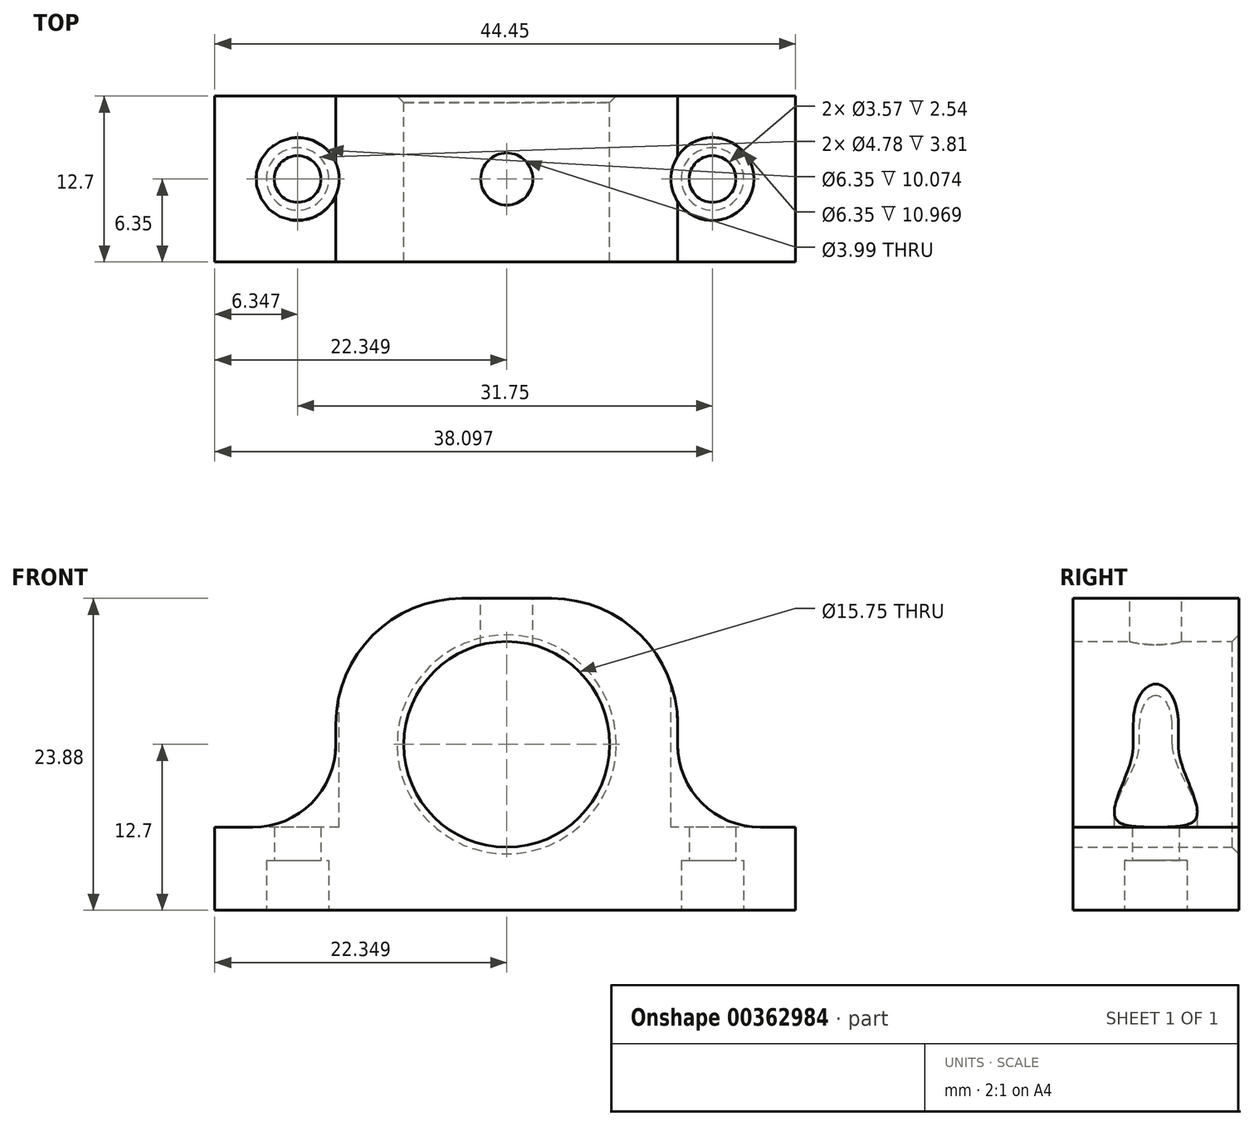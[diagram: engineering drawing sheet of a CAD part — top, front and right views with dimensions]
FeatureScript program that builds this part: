
annotation { "Feature Type Name" : "Feature", "Feature Type Description" : "" }
export const myFeature = defineFeature(function(context is Context, id is Id, definition is map)
    precondition{}
    {
        {
            var Q0;
            Q0=qCreatedBy(makeId("Front.planeOp"),FACE);
            var sketch = newSketch(context, id + "F0", { "sketchPlane" : qUnion([Q0])});
            skLineSegment(sketch, "E0", {"start": v(-60.83, 8) * mm, "end": v(-16.38, 8) * mm});
            skLineSegment(sketch, "E1", {"start": v(-16.38, 8) * mm, "end": v(-16.38, 14.34) * mm});
            skLineSegment(sketch, "E2", {"start": v(-60.83, 8) * mm, "end": v(-60.83, 14.34) * mm});
            skCircle(sketch, "E3", {"center": v(-38.48, 20.7) * mm, "radius": 7.87 * mm});
            skLineSegment(sketch, "E4.0", {"start": v(-25.4, 20.7) * mm, "end": v(-25.4, 22.21) * mm});
            skLineSegment(sketch, "E5.0", {"start": v(-51.56, 20.7) * mm, "end": v(-51.56, 22.21) * mm});
            skLineSegment(sketch, "E6", {"start": v(-57.91, 14.34) * mm, "end": v(-60.83, 14.34) * mm});
            skLineSegment(sketch, "E7", {"start": v(-19.05, 14.34) * mm, "end": v(-16.38, 14.34) * mm});
            skLineSegment(sketch, "E8.0", {"start": v(-41.9, 31.87) * mm, "end": v(-35.05, 31.87) * mm});
            skArc(sketch, "E9.filletArc", {"start": v(-41.9, 31.87) * mm, "mid": v(-48.73, 29.04) * mm, "end": v(-51.56, 22.21) * mm});
            skArc(sketch, "E10.filletArc", {"start": v(-25.4, 22.21) * mm, "mid": v(-28.23, 29.04) * mm, "end": v(-35.05, 31.87) * mm});
            skPoint(sketch, "E11.visualSharp", {"position": v(-25.4, 14.34) * mm});
            skArc(sketch, "E11.filletArc", {"start": v(-25.4, 20.7) * mm, "mid": v(-23.54, 16.2) * mm, "end": v(-19.05, 14.34) * mm});
            skPoint(sketch, "E12.visualSharp", {"position": v(-51.56, 14.34) * mm});
            skArc(sketch, "E12.filletArc", {"start": v(-57.91, 14.34) * mm, "mid": v(-53.42, 16.2) * mm, "end": v(-51.56, 20.7) * mm});
            skSolve(sketch);
        }
        {
            var Q0;
            Q0=makeQuery(id+"F0.imprint","IMPRINT",FACE,{"disambiguationData":[TD([[makeQuery(id+"F0.imprint","IMPRINT",EDGE,{"derivedFrom":sQuery(id+"F0.wireOp",EDGE,"E0")}),1.0]])]});
            extrude(context, id + "F1", {"entities" : qUnion([Q0]), "depth" : 12.7 * mm});
        }
        {
            var Q0;
            Q0=makeQuery(id+"F1.opExtrude","SWEPT_FACE",FACE,{"disambiguationData":[OSD([sQuery(id+"F0.wireOp",EDGE,"E0")])]});
            var sketch = newSketch(context, id + "F2", { "sketchPlane" : qUnion([Q0])});
            skPoint(sketch, "E13", {"position": v(-54.48, 6.35) * mm});
            skPoint(sketch, "E13.positionSnap0", {"position": v(-60.83, 6.35) * mm});
            skPoint(sketch, "E14", {"position": v(-22.73, 6.35) * mm});
            skCircle(sketch, "E15", {"center": v(-54.48, 6.35) * mm, "radius": 2.39 * mm});
            skCircle(sketch, "E16", {"center": v(-22.73, 6.35) * mm, "radius": 2.39 * mm});
            skSolve(sketch);
        }
        {
            var Q0;
            Q0=sQuery(id+"F2.wireOp",VERTEX,"E13");
            var Q1;
            Q1=sQuery(id+"F2.wireOp",VERTEX,"E14");
            var Q2;
            Q2=makeQuery(id+"F1.opExtrude","SWEPT_BODY",BODY,{"disambiguationData":[OSD([sQuery(id+"F0.wireOp",EDGE,"E0"),sQuery(id+"F0.wireOp",EDGE,"E1"),sQuery(id+"F0.wireOp",EDGE,"E2"),sQuery(id+"F0.wireOp",EDGE,"E3"),sQuery(id+"F0.wireOp",EDGE,"E4.0"),sQuery(id+"F0.wireOp",EDGE,"E5.0"),sQuery(id+"F0.wireOp",EDGE,"E6"),sQuery(id+"F0.wireOp",EDGE,"E7"),sQuery(id+"F0.wireOp",EDGE,"E8.0"),sQuery(id+"F0.wireOp",EDGE,"E9.filletArc"),sQuery(id+"F0.wireOp",EDGE,"E10.filletArc"),sQuery(id+"F0.wireOp",EDGE,"E11.filletArc"),sQuery(id+"F0.wireOp",EDGE,"E12.filletArc")])]});
            hole(context, id + "F3", {"style" : HoleStyle.SIMPLE, "endStyle" : HoleEndStyle.THROUGH, "standardTappedOrClearance" : lookupTablePath({ "standard" : "ANSI", "size" : "#28 (0.14)", "type" : "Drilled" }), "standardBlindInLast" : lookupTablePath({ "standard" : "ANSI", "size" : "#28", "type" : "Drilled" }), "holeDiameter" : 3.57 * mm, "tappedDepth" : 5.4 * mm, "tapClearance" : 3, "locations" : qUnion([Q0, Q1]), "scope" : qUnion([Q2])});
        }
        {
            var Q0;
            Q0=makeQuery(id+"F2.imprint","IMPRINT",FACE,{"disambiguationData":[TD([[makeQuery(id+"F2.imprint","IMPRINT",EDGE,{"derivedFrom":sQuery(id+"F2.wireOp",EDGE,"E15")}),1.0]])]});
            var Q1;
            Q1=makeQuery(id+"F2.imprint","IMPRINT",FACE,{"disambiguationData":[TD([[makeQuery(id+"F2.imprint","IMPRINT",EDGE,{"derivedFrom":sQuery(id+"F2.wireOp",EDGE,"E16")}),1.0]])]});
            extrude(context, id + "F4", {"entities" : qUnion([Q0, Q1]), "operationType" : NewBodyOperationType.REMOVE, "oppositeDirection" : true, "depth" : 3.8 * mm});
        }
        {
            var Q0;
            Q0=makeQuery(id+"F1.opExtrude","SWEPT_FACE",FACE,{"disambiguationData":[OSD([sQuery(id+"F0.wireOp",EDGE,"E6")])]});
            cPlane(context, id + "F5", {"entities" : qUnion([Q0]), "cplaneType" : CPlaneType.OFFSET, "offset" : 12.7 * mm, "width" : 152.4 * mm, "height" : 152.4 * mm});
        }
        {
            var Q0;
            Q0=qCreatedBy(id+"F5.planeOp",FACE);
            var sketch = newSketch(context, id + "F6", { "sketchPlane" : qUnion([Q0])});
            skPoint(sketch, "E17.0", {"position": v(-54.48, -6.35) * mm});
            skPoint(sketch, "E18.0", {"position": v(-22.73, -6.35) * mm});
            skCircle(sketch, "E19", {"center": v(-54.48, -6.35) * mm, "radius": 3.18 * mm});
            skCircle(sketch, "E20", {"center": v(-22.73, -6.35) * mm, "radius": 3.18 * mm});
            skSolve(sketch);
        }
        {
            var Q0;
            Q0=makeQuery(id+"F6.imprint","IMPRINT",FACE,{"disambiguationData":[TD([[makeQuery(id+"F6.imprint","IMPRINT",EDGE,{"derivedFrom":sQuery(id+"F6.wireOp",EDGE,"E19")}),1.0]])]});
            var Q1;
            Q1=makeQuery(id+"F6.imprint","IMPRINT",FACE,{"disambiguationData":[TD([[makeQuery(id+"F6.imprint","IMPRINT",EDGE,{"derivedFrom":sQuery(id+"F6.wireOp",EDGE,"E20")}),1.0]])]});
            extrude(context, id + "F7", {"entities" : qUnion([Q0, Q1]), "operationType" : NewBodyOperationType.REMOVE, "oppositeDirection" : true, "depth" : 12.7 * mm});
        }
        {
            var Q0;
            Q0=makeQuery(id+"F1.opExtrude","SWEPT_FACE",FACE,{"disambiguationData":[OSD([sQuery(id+"F0.wireOp",EDGE,"E8.0")])]});
            var sketch = newSketch(context, id + "F8", { "sketchPlane" : qUnion([Q0])});
            skPoint(sketch, "E21", {"position": v(-38.48, -6.35) * mm});
            skPoint(sketch, "E21.positionSnap0", {"position": v(-41.9, -6.35) * mm});
            skPoint(sketch, "E21.positionSnap1", {"position": v(-38.48, 0) * mm});
            skSolve(sketch);
        }
        {
            var Q0;
            Q0=sQuery(id+"F8.wireOp",VERTEX,"E21");
            var Q1;
            Q1=makeQuery(id+"F1.opExtrude","SWEPT_BODY",BODY,{"disambiguationData":[OSD([sQuery(id+"F0.wireOp",EDGE,"E0"),sQuery(id+"F0.wireOp",EDGE,"E1"),sQuery(id+"F0.wireOp",EDGE,"E2"),sQuery(id+"F0.wireOp",EDGE,"E3"),sQuery(id+"F0.wireOp",EDGE,"E4.0"),sQuery(id+"F0.wireOp",EDGE,"E5.0"),sQuery(id+"F0.wireOp",EDGE,"E6"),sQuery(id+"F0.wireOp",EDGE,"E7"),sQuery(id+"F0.wireOp",EDGE,"E8.0"),sQuery(id+"F0.wireOp",EDGE,"E9.filletArc"),sQuery(id+"F0.wireOp",EDGE,"E10.filletArc"),sQuery(id+"F0.wireOp",EDGE,"E11.filletArc"),sQuery(id+"F0.wireOp",EDGE,"E12.filletArc")])]});
            hole(context, id + "F9", {"style" : HoleStyle.SIMPLE, "endStyle" : HoleEndStyle.BLIND, "standardTappedOrClearance" : lookupTablePath({ "standard" : "ANSI", "size" : "#22 (0.16)", "type" : "Drilled" }), "standardBlindInLast" : lookupTablePath({ "standard" : "ANSI", "size" : "#22", "type" : "Drilled" }), "holeDiameter" : 4 * mm, "holeDepth" : 6.35 * mm, "tappedDepth" : 5.4 * mm, "tapClearance" : 3, "locations" : qUnion([Q0]), "scope" : qUnion([Q1])});
        }
        {
            var Q0;
            Q0=makeQuery(id+"F1.opExtrude","CAP_EDGE",EDGE,{"disambiguationData":[OSD([sQuery(id+"F0.wireOp",EDGE,"E3")])],"isStart":true});
            chamfer(context, id + "F10", {"entities" : qUnion([Q0]), "chamferType" : ChamferType.OFFSET_ANGLE, "width" : 0.5 * mm, "oppositeDirection" : false, "angle" : 45 * degree, "tangentPropagation" : true});
        }
    });
